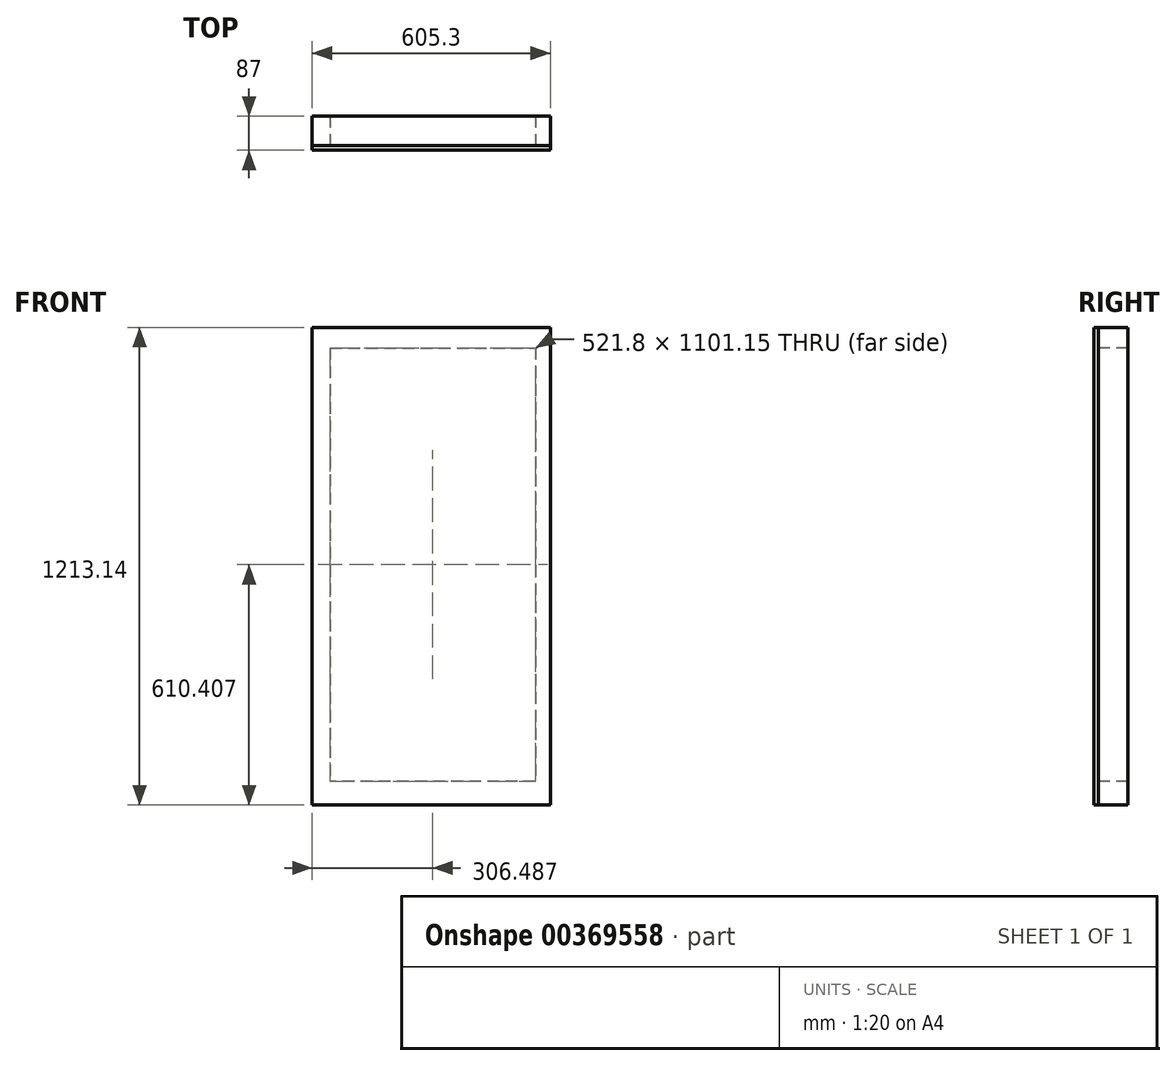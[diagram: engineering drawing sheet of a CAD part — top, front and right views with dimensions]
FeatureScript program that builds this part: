
annotation { "Feature Type Name" : "Feature", "Feature Type Description" : "" }
export const myFeature = defineFeature(function(context is Context, id is Id, definition is map)
    precondition{}
    {
        {
            var Q0;
            Q0=qCreatedBy(makeId("Front.planeOp"),FACE);
            var sketch = newSketch(context, id + "F0", { "sketchPlane" : qUnion([Q0])});
            skLineSegment(sketch, "E0.bottom", {"start": v(302.65, 606.57) * mm, "end": v(-302.65, 606.57) * mm});
            skLineSegment(sketch, "E0.top", {"start": v(302.65, -606.57) * mm, "end": v(-302.65, -606.57) * mm});
            skLineSegment(sketch, "E0.left", {"start": v(302.65, 606.57) * mm, "end": v(302.65, -606.57) * mm});
            skLineSegment(sketch, "E0.right", {"start": v(-302.65, 606.57) * mm, "end": v(-302.65, -606.57) * mm});
            skPoint(sketch, "E0.middle", {"position": v(0, 0) * mm});
            skSolve(sketch);
        }
        {
            var Q0;
            Q0 = qSketchRegion(id + "F0", true);
            extrude(context, id + "F1", {"entities" : qUnion([Q0]), "depth" : 12 * mm});
        }
        {
            var Q0;
            Q0=makeQuery(id+"F1.opExtrude","CAP_FACE",FACE,{"disambiguationData":[OSD([sQuery(id+"F0.wireOp",EDGE,"E0.bottom"),sQuery(id+"F0.wireOp",EDGE,"E0.top"),sQuery(id+"F0.wireOp",EDGE,"E0.left"),sQuery(id+"F0.wireOp",EDGE,"E0.right")])],"isStart":true});
            var sketch = newSketch(context, id + "F2", { "sketchPlane" : qUnion([Q0])});
            skLineSegment(sketch, "E1.bottom", {"start": v(-302.65, 606.57) * mm, "end": v(-264.74, 606.57) * mm});
            skLineSegment(sketch, "E1.top", {"start": v(-302.65, -606.57) * mm, "end": v(-264.74, -606.57) * mm});
            skLineSegment(sketch, "E1.left", {"start": v(-302.65, 606.57) * mm, "end": v(-302.65, -606.57) * mm});
            skLineSegment(sketch, "E1.right", {"start": v(-264.74, 606.57) * mm, "end": v(-264.74, -606.57) * mm});
            skLineSegment(sketch, "E2.bottom", {"start": v(257.06, 606.57) * mm, "end": v(302.65, 606.57) * mm});
            skLineSegment(sketch, "E2.top", {"start": v(257.06, -606.57) * mm, "end": v(302.65, -606.57) * mm});
            skLineSegment(sketch, "E2.left", {"start": v(257.06, 606.57) * mm, "end": v(257.06, -606.57) * mm});
            skLineSegment(sketch, "E2.right", {"start": v(302.65, 606.57) * mm, "end": v(302.65, -606.57) * mm});
            skLineSegment(sketch, "E3.bottom", {"start": v(257.06, 554.41) * mm, "end": v(-264.74, 554.41) * mm});
            skLineSegment(sketch, "E3.top", {"start": v(257.06, 606.57) * mm, "end": v(-264.74, 606.57) * mm});
            skLineSegment(sketch, "E3.left", {"start": v(257.06, 554.41) * mm, "end": v(257.06, 606.57) * mm});
            skLineSegment(sketch, "E3.right", {"start": v(-264.74, 554.41) * mm, "end": v(-264.74, 606.57) * mm});
            skLineSegment(sketch, "E4.bottom", {"start": v(-264.74, -546.74) * mm, "end": v(257.06, -546.74) * mm});
            skLineSegment(sketch, "E4.top", {"start": v(-264.74, -606.57) * mm, "end": v(257.06, -606.57) * mm});
            skLineSegment(sketch, "E4.left", {"start": v(-264.74, -546.74) * mm, "end": v(-264.74, -606.57) * mm});
            skLineSegment(sketch, "E4.right", {"start": v(257.06, -546.74) * mm, "end": v(257.06, -606.57) * mm});
            skSolve(sketch);
        }
        {
            var Q0;
            Q0 = qSketchRegion(id + "F2", true);
            extrude(context, id + "F3", {"entities" : qUnion([Q0]), "depth" : 75 * mm});
        }
    });
